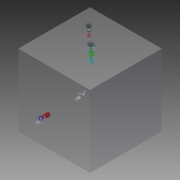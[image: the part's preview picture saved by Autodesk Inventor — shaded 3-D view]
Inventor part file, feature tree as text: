
AUTODESK INVENTOR PART (.ipt)
format: ipt  version: 2014 (Build 180170000, 170)  size: 321,024 bytes
history: native  units: mm
features: other x57, sketch x14, extrude x1
ambient origin geometry x8: Origin, YZ Plane, XZ Plane, XY Plane, X Axis, Y Axis, Z Axis, Center Point
bodies: 实体1 (feature_tree)
feature tree (72):
  extrude  "拉伸1"  TaperAngle=0.0deg  [1 undecoded]
  other  "UCS1"
  other  "UCS2"
  other  "UCS3"
  other  "UCS4"
  other  "UCS5"
  other  "UCS6"
  sketch  "草图1"  dims[d0=300.0mm d1=0.0mm]
  sketch  "草图7"  dims[d8=0.0mm d9=0.0mm d10=0.0mm d11=0.0mm d12=0.0mm d13=0.0mm]
  other  "曲面3"
  sketch  "草图8"  dims[d14=0.0mm d15=0.0mm d16=0.0mm d17=0.0mm d18=0.0mm d19=0.0mm]
  other  "曲面4"
  sketch  "草图9"  dims[d20=0.0mm d21=0.0mm d22=0.0mm d23=0.0mm d24=0.0mm d25=0.0mm]
  other  "曲面5"
  sketch  "草图11"  dims[d32=0.0mm d33=0.0mm d34=0.0mm d35=0.0mm d36=0.0mm d37=0.0mm d38=0.0mm]
  other  "曲面6"
  sketch  "草图12"  dims[d45=0.0mm]
  other  "曲面7"
  sketch  "草图14"  dims[d53=0.0mm]
  other  "曲面8"
  sketch  "草图15"  dims[d57=-48.42mm]
  other  "曲面9"
  sketch  "草图17"  dims[d60=-31.75mm]
  other  "曲面10"
  sketch  "草图18"  dims[d61=13.5mm d62=0.0mm d63=-15.07mm d64=3.18mm d65=0.0mm d66=0.0mm d70=-30.09mm d71=0.13mm d72=0.0mm d73=-15.07mm d74=6.35mm d75=0.0mm d76=0.0mm d80=-30.09mm d81=0.13mm d82=0.0mm d83=-15.07mm d84=6.35mm d85=0.0mm d86=0.0mm d90=-31.29mm d91=0.13mm d92=0.0mm d93=-17.79mm d94=5.0mm d95=0.0mm]
  other  "曲面11"
  other  "UCS1: YZ 平面"
  other  "UCS1: XZ 平面"
  other  "UCS1: XY 平面"
  other  "UCS1: X 轴"
  other  "UCS1: Y 轴"
  other  "UCS1: Z 轴"
  other  "UCS1: 原点"
  other  "UCS2: YZ 平面"
  other  "UCS2: XZ 平面"
  other  "UCS2: XY 平面"
  other  "UCS2: X 轴"
  other  "UCS2: Y 轴"
  other  "UCS2: Z 轴"
  other  "UCS2: 原点"
  other  "UCS3: YZ 平面"
  other  "UCS3: XZ 平面"
  other  "UCS3: XY 平面"
  other  "UCS3: X 轴"
  other  "UCS3: Y 轴"
  other  "UCS3: Z 轴"
  other  "UCS3: 原点"
  other  "UCS4: YZ 平面"
  other  "UCS4: XZ 平面"
  other  "UCS4: XY 平面"
  other  "UCS4: X 轴"
  other  "UCS4: Y 轴"
  other  "UCS4: Z 轴"
  other  "UCS4: 原点"
  other  "UCS5: YZ 平面"
  other  "UCS5: XZ 平面"
  other  "UCS5: XY 平面"
  other  "UCS5: X 轴"
  other  "UCS5: Y 轴"
  other  "UCS5: Z 轴"
  other  "UCS5: 原点"
  other  "UCS6: YZ 平面"
  other  "UCS6: XZ 平面"
  other  "UCS6: XY 平面"
  other  "UCS6: X 轴"
  other  "UCS6: Y 轴"
  other  "UCS6: Z 轴"
  other  "UCS6: 原点"
  sketch  "草图6"  dims[d2=0.0mm d3=0.0mm d4=0.0mm d5=0.0mm d6=0.0mm d7=0.0mm]
  sketch  "草图10"  dims[d26=0.0mm d27=0.0mm d28=0.0mm d29=0.0mm d30=0.0mm d31=0.0mm]
  sketch  "草图13"  dims[d52=0.0mm]
  sketch  "草图16"  dims[d58=0.13mm d59=0.0mm]
note: 1 required parameter value undecoded (feature->parameter linkage not recoverable at this tier; creation-order binding heuristic only, values carry confidence <= 0.55)
